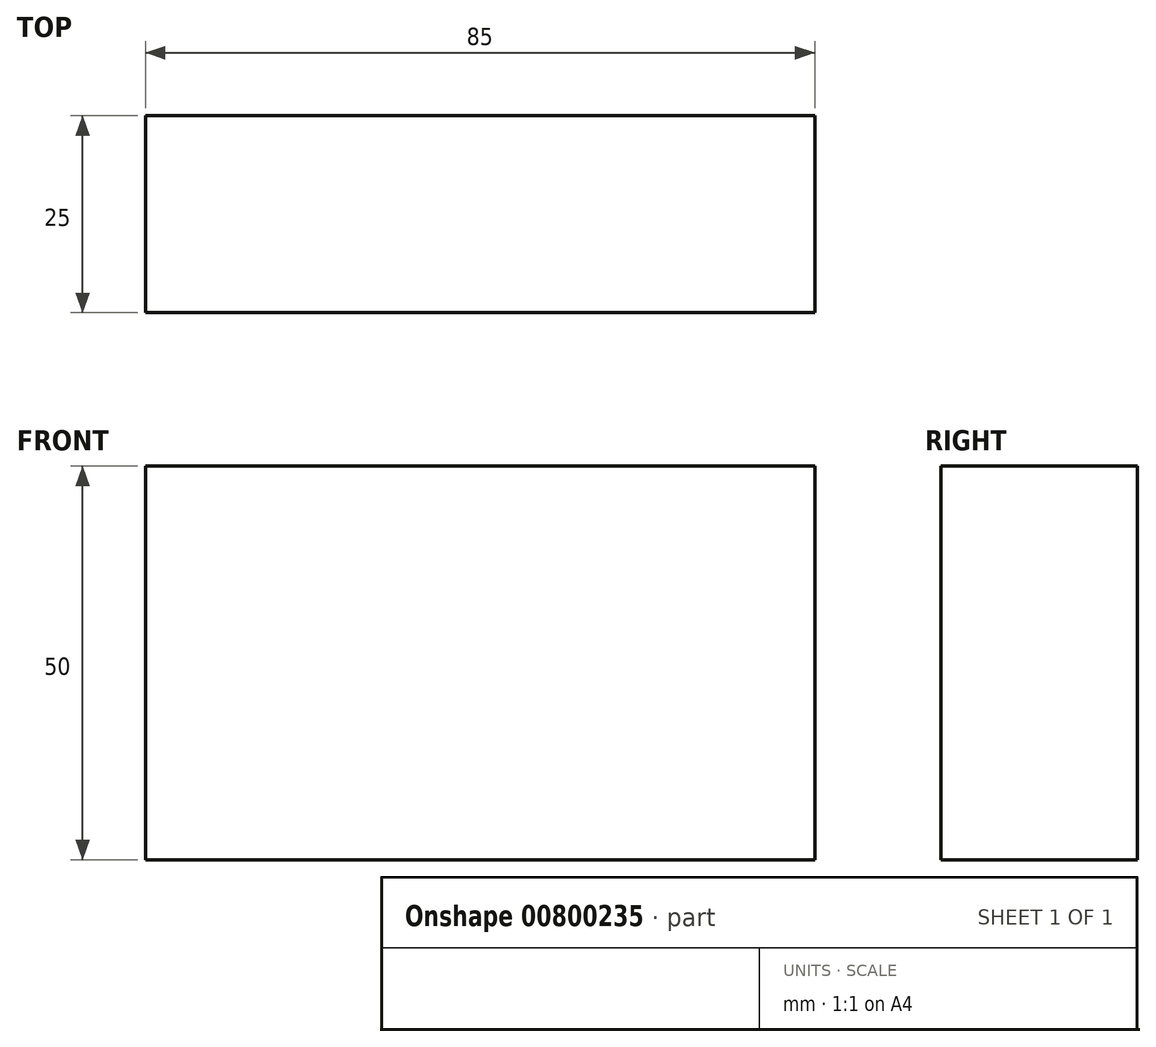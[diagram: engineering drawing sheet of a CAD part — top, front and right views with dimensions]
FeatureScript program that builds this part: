
annotation { "Feature Type Name" : "Feature", "Feature Type Description" : "" }
export const myFeature = defineFeature(function(context is Context, id is Id, definition is map)
    precondition{}
    {
        {
            var Q0;
            Q0=qCreatedBy(makeId("Front.planeOp"),FACE);
            var sketch = newSketch(context, id + "F0", { "sketchPlane" : qUnion([Q0])});
            skLineSegment(sketch, "E0.bottom", {"start": v(-42.5, 25) * mm, "end": v(42.5, 25) * mm});
            skLineSegment(sketch, "E0.top", {"start": v(-42.5, -25) * mm, "end": v(42.5, -25) * mm});
            skLineSegment(sketch, "E0.left", {"start": v(-42.5, 25) * mm, "end": v(-42.5, -25) * mm});
            skLineSegment(sketch, "E0.right", {"start": v(42.5, 25) * mm, "end": v(42.5, -25) * mm});
            skPoint(sketch, "E0.middle", {"position": v(0, 0) * mm});
            skSolve(sketch);
        }
        {
            var Q0;
            Q0 = qSketchRegion(id + "F0", true);
            extrude(context, id + "F1", {"entities" : qUnion([Q0]), "depth" : 25 * mm, "offsetDistance" : 25 * mm});
        }
    });
